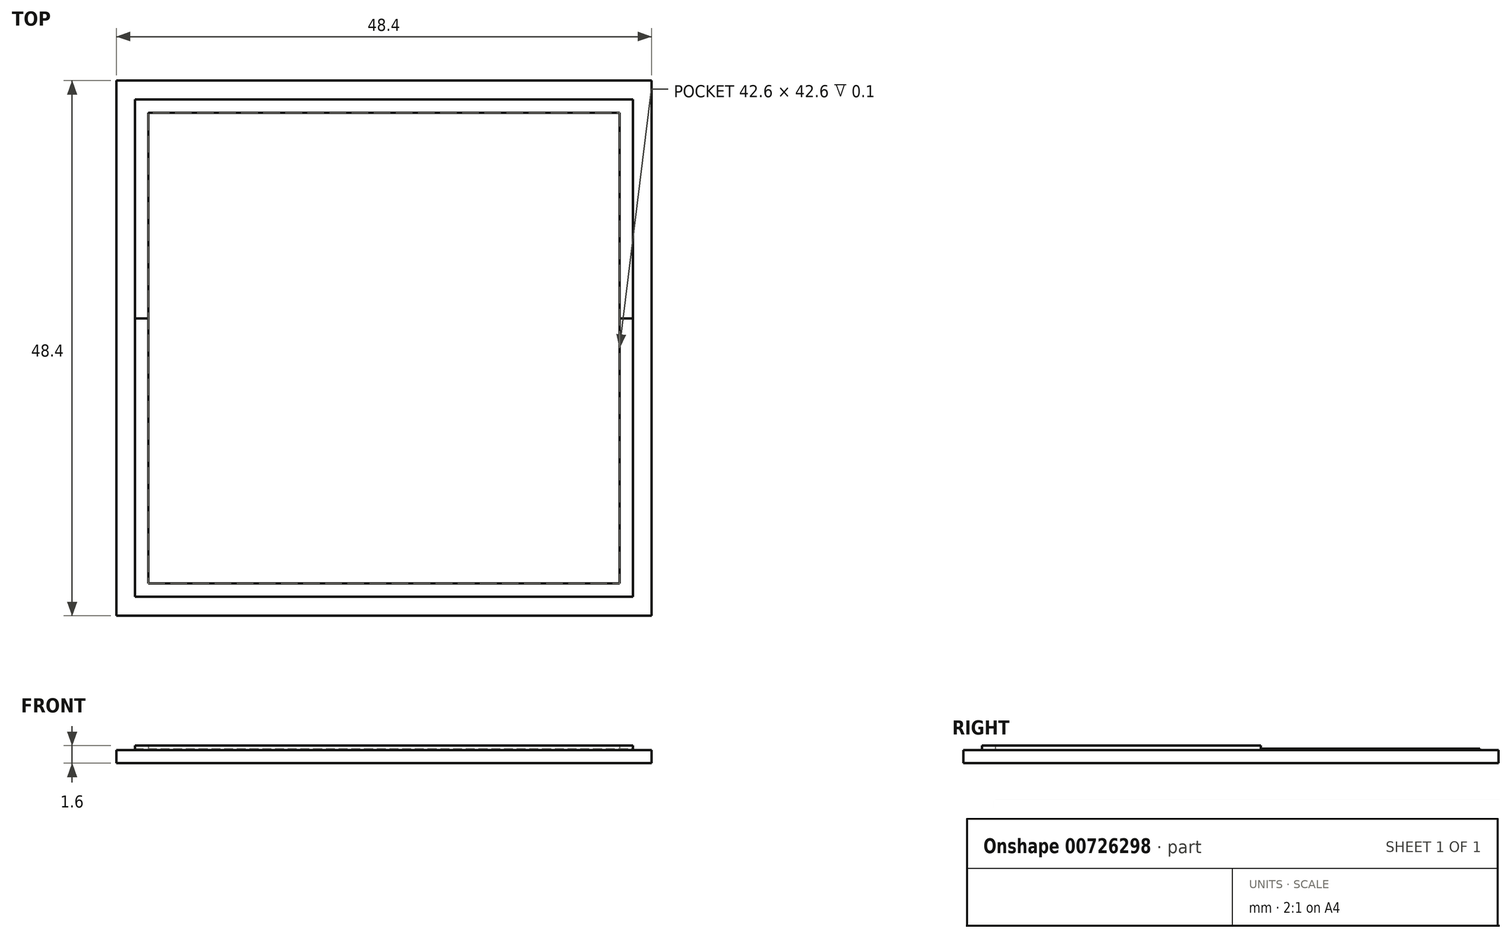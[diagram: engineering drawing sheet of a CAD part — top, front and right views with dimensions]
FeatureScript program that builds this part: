
annotation { "Feature Type Name" : "Feature", "Feature Type Description" : "" }
export const myFeature = defineFeature(function(context is Context, id is Id, definition is map)
    precondition{}
    {
        {
            var Q0;
            Q0=qCreatedBy(makeId("Top.planeOp"),FACE);
            var sketch = newSketch(context, id + "F0", { "sketchPlane" : qUnion([Q0])});
            skLineSegment(sketch, "E0.bottom", {"start": v(-24.2, 23.81) * mm, "end": v(24.2, 23.81) * mm});
            skLineSegment(sketch, "E0.top", {"start": v(-24.2, -24.59) * mm, "end": v(24.2, -24.59) * mm});
            skLineSegment(sketch, "E0.left", {"start": v(-24.2, 23.81) * mm, "end": v(-24.2, -24.59) * mm});
            skLineSegment(sketch, "E0.right", {"start": v(24.2, 23.81) * mm, "end": v(24.2, -24.59) * mm});
            skLineSegment(sketch, "E1.bottom", {"start": v(-22.5, 22.11) * mm, "end": v(22.5, 22.11) * mm});
            skLineSegment(sketch, "E1.top", {"start": v(-22.5, -22.89) * mm, "end": v(22.5, -22.89) * mm});
            skLineSegment(sketch, "E1.left", {"start": v(-22.5, 22.11) * mm, "end": v(-22.5, -22.89) * mm});
            skLineSegment(sketch, "E1.right", {"start": v(22.5, 22.11) * mm, "end": v(22.5, -22.89) * mm});
            skLineSegment(sketch, "E2.bottom", {"start": v(-21.3, 20.91) * mm, "end": v(21.3, 20.91) * mm});
            skLineSegment(sketch, "E2.top", {"start": v(-21.3, -21.69) * mm, "end": v(21.3, -21.69) * mm});
            skLineSegment(sketch, "E2.left", {"start": v(-21.3, 20.91) * mm, "end": v(-21.3, -21.69) * mm});
            skLineSegment(sketch, "E2.right", {"start": v(21.3, 20.91) * mm, "end": v(21.3, -21.69) * mm});
            skLineSegment(sketch, "E3", {"start": v(-22.5, 2.31) * mm, "end": v(-21.3, 2.31) * mm});
            skLineSegment(sketch, "E4", {"start": v(21.3, 2.31) * mm, "end": v(22.5, 2.31) * mm});
            skSolve(sketch);
        }
        {
            var Q0;
            Q0=qCreatedBy(makeId("Top.planeOp"),FACE);
            var sketch = newSketch(context, id + "F1", { "sketchPlane" : qUnion([Q0])});
            skLineSegment(sketch, "E5.bottom", {"start": v(-24.2, 23.81) * mm, "end": v(24.2, 23.81) * mm});
            skLineSegment(sketch, "E5.top", {"start": v(-24.2, -24.59) * mm, "end": v(24.2, -24.59) * mm});
            skLineSegment(sketch, "E5.left", {"start": v(-24.2, 23.81) * mm, "end": v(-24.2, -24.59) * mm});
            skLineSegment(sketch, "E5.right", {"start": v(24.2, 23.81) * mm, "end": v(24.2, -24.59) * mm});
            skLineSegment(sketch, "E6.bottom", {"start": v(-22.5, 22.11) * mm, "end": v(22.5, 22.11) * mm});
            skLineSegment(sketch, "E6.top", {"start": v(-22.5, -22.89) * mm, "end": v(22.5, -22.89) * mm});
            skLineSegment(sketch, "E6.left", {"start": v(-22.5, 22.11) * mm, "end": v(-22.5, -22.89) * mm});
            skLineSegment(sketch, "E6.right", {"start": v(22.5, 22.11) * mm, "end": v(22.5, -22.89) * mm});
            skLineSegment(sketch, "E7.bottom", {"start": v(-21.3, 20.91) * mm, "end": v(21.3, 20.91) * mm});
            skLineSegment(sketch, "E7.top", {"start": v(-21.3, -21.69) * mm, "end": v(21.3, -21.69) * mm});
            skLineSegment(sketch, "E7.left", {"start": v(-21.3, 20.91) * mm, "end": v(-21.3, -21.69) * mm});
            skLineSegment(sketch, "E7.right", {"start": v(21.3, 20.91) * mm, "end": v(21.3, -21.69) * mm});
            skLineSegment(sketch, "E8", {"start": v(-22.5, 2.31) * mm, "end": v(-21.3, 2.31) * mm});
            skLineSegment(sketch, "E9", {"start": v(21.3, 2.31) * mm, "end": v(22.5, 2.31) * mm});
            skSolve(sketch);
        }
        {
            var Q0;
            Q0=qCreatedBy(makeId("Top.planeOp"),FACE);
            var sketch = newSketch(context, id + "F2", { "sketchPlane" : qUnion([Q0])});
            skLineSegment(sketch, "E10.bottom", {"start": v(-24.2, 23.81) * mm, "end": v(24.2, 23.81) * mm});
            skLineSegment(sketch, "E10.top", {"start": v(-24.2, -24.59) * mm, "end": v(24.2, -24.59) * mm});
            skLineSegment(sketch, "E10.left", {"start": v(-24.2, 23.81) * mm, "end": v(-24.2, -24.59) * mm});
            skLineSegment(sketch, "E10.right", {"start": v(24.2, 23.81) * mm, "end": v(24.2, -24.59) * mm});
            skLineSegment(sketch, "E11.bottom", {"start": v(-22.5, 22.11) * mm, "end": v(22.5, 22.11) * mm});
            skLineSegment(sketch, "E11.top", {"start": v(-22.5, -22.89) * mm, "end": v(22.5, -22.89) * mm});
            skLineSegment(sketch, "E11.left", {"start": v(-22.5, 22.11) * mm, "end": v(-22.5, -22.89) * mm});
            skLineSegment(sketch, "E11.right", {"start": v(22.5, 22.11) * mm, "end": v(22.5, -22.89) * mm});
            skLineSegment(sketch, "E12.bottom", {"start": v(-21.3, 20.91) * mm, "end": v(21.3, 20.91) * mm});
            skLineSegment(sketch, "E12.top", {"start": v(-21.3, -21.69) * mm, "end": v(21.3, -21.69) * mm});
            skLineSegment(sketch, "E12.left", {"start": v(-21.3, 20.91) * mm, "end": v(-21.3, -21.69) * mm});
            skLineSegment(sketch, "E12.right", {"start": v(21.3, 20.91) * mm, "end": v(21.3, -21.69) * mm});
            skLineSegment(sketch, "E13", {"start": v(-22.5, 2.31) * mm, "end": v(-21.3, 2.31) * mm});
            skLineSegment(sketch, "E14", {"start": v(21.3, 2.31) * mm, "end": v(22.5, 2.31) * mm});
            skSolve(sketch);
        }
        {
            var Q0;
            {var subQ2=sQuery(id+"F0.wireOp",EDGE,"E1.top");Q0=makeQuery(id+"F0.imprint","IMPRINT",FACE,{"disambiguationData":[TD([[makeQuery(id+"F0.imprint","IMPRINT",EDGE,{"derivedFrom":subQ2}),1.0]])]});}
            extrude(context, id + "F3", {"entities" : qUnion([Q0]), "depth" : 1.6 * mm, "offsetDistance" : 25 * mm});
        }
        {
            var Q0;
            {var subQ2=sQuery(id+"F1.wireOp",EDGE,"E6.bottom");Q0=makeQuery(id+"F1.imprint","IMPRINT",FACE,{"disambiguationData":[TD([[makeQuery(id+"F1.imprint","IMPRINT",EDGE,{"derivedFrom":subQ2}),-1.0]])]});}
            extrude(context, id + "F4", {"entities" : qUnion([Q0]), "operationType" : NewBodyOperationType.ADD, "depth" : 1.3 * mm, "offsetDistance" : 25 * mm});
        }
        {
            var Q0;
            Q0 = qSketchRegion(id + "F2", true);
            var Q1;
            {var subQ3=sQuery(id+"F2.wireOp",EDGE,"E12.bottom");Q1=makeQuery(id+"F2.imprint","IMPRINT",FACE,{"disambiguationData":[TD([[makeQuery(id+"F2.imprint","IMPRINT",EDGE,{"derivedFrom":subQ3}),-1.0]])]});}
            extrude(context, id + "F5", {"entities" : qUnion([Q0, Q1]), "operationType" : NewBodyOperationType.ADD, "depth" : 1.2 * mm, "offsetDistance" : 25 * mm});
        }
    });
